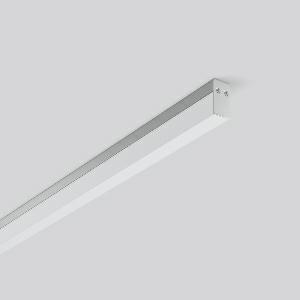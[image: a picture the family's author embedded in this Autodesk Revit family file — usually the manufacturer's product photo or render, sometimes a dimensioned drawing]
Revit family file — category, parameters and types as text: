
# Revit family: less_is_more_21_312239_000_0315
name_source: partatom
category: Lighting Fixtures
units: mm (PartAtom-declared; Revit-internal decimal feet)

## family parameters
Cut with Voids When Loaded = No
Host = Face
Light Source = No
Part Type = Normal
Room Calculation Point = No
Round Connector Dimension = Use Diameter
Shared = No

## types (1)
- LESS IS MORE 21 (1 x LED Modul 830, 2550 lm, 3000)
    Apparent Load = 25 VA
    CIE Flux Codes = 33 62 84 72 100
    Color Rendering = 80
    Color Temperature = 3000
    Default Elevation = 1800 mm
    Description = Series: LESS IS MORE 21
Minimalist ceiling and wall luminaire with light emission on three sides. Housing: extruded aluminium profile, anodised or powder-coated. End cap anodised aluminium or powder-coated. Diffuser made of non-yellowing plastic (PMMA), opal. Suitable for Ceiling mounting, Wall (surface). External driver with connecting cable. 
Colour: anodised aluminium
Length: 1508 mm
Width: 21 mm
Height: 36 mm
Lamp: LED
Socket: without socket
Colour temperature: 3000K
Colour rendering index (CRI): 80
System power: 25 W
Rated luminous flux: 2550 lm
Luminous efficiency: 102 lm/W
Control gear: Constant voltage supply
Protection class: II
Type of protection: IP 20
    Height = 36 mm
    Lamp = 1 x LED Modul 830
    Lamp Light Flux = 2550 lm
    Lamp count = 1
    Length = 1508 mm
    Lifetime = 50000 h
    Luminous efficacy = 102 lm/W
    Manufacturer = RZB
    ModVariant = No
    Model = 312239.000
    Mounting Place = Ceiling, Wall
    Mounting Type = Surface mounted
    Number of Poles = 1
    OnlyDefault = Yes
    Power Factor = 1
    Product Name = LESS IS MORE 21
    Product group = Surface mounted LED linear luminaires
    ProductGroupID = 307
    Protection Class = Protection class II
    Protection Degree = IP 20
    RLX_Detail_Level = 1
    RLX_Emergency_Light_Flux = 0 lm
    RLX_Emergency_Type = 0
    RLX_Emergency_Type_DB = No
    RlxData = <blob elided: 31853 chars, md5=dfc60c98>
    Socket = socket
    Standby Power = 0 W
    System Light Flux = 2550 lm
    System Power = 25 W
    Type Comments = Product without accessories
    Type Image = 312237.000.jpg
    URL = http://relux.com
    VarID = ---
    Voltage = 230 V
    Voltage Range = 220-240 V
    Weight = 0.00 kg
    Width = 21 mm

## geometry (parser evidence)
native form markers: Blend x4, Sweep x13
no freeform markers — native parametric forms only
